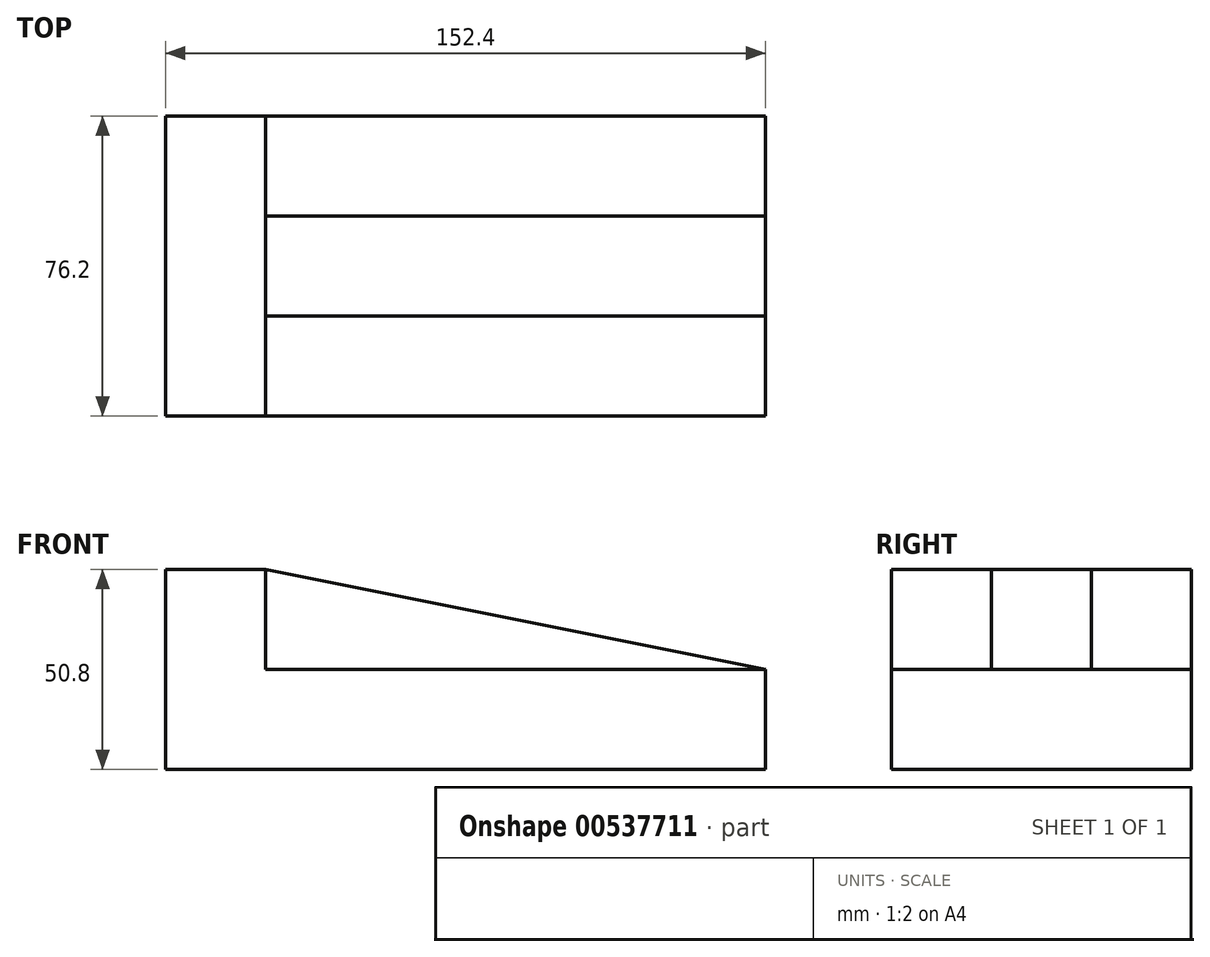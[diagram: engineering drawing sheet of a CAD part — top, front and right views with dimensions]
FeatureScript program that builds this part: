
annotation { "Feature Type Name" : "Feature", "Feature Type Description" : "" }
export const myFeature = defineFeature(function(context is Context, id is Id, definition is map)
    precondition{}
    {
        {
            var Q0;
            Q0=qCreatedBy(makeId("Front.planeOp"),FACE);
            var sketch = newSketch(context, id + "F0", { "sketchPlane" : qUnion([Q0])});
            skLineSegment(sketch, "E0.bottom", {"start": v(-87.33, 25.9) * mm, "end": v(-61.93, 25.9) * mm});
            skLineSegment(sketch, "E0.top", {"start": v(-87.33, -24.9) * mm, "end": v(65.07, -24.9) * mm});
            skLineSegment(sketch, "E0.left", {"start": v(-87.33, 25.9) * mm, "end": v(-87.33, -24.9) * mm});
            skLineSegment(sketch, "E0.right", {"start": v(65.07, 0.5) * mm, "end": v(65.07, -24.9) * mm});
            skLineSegment(sketch, "E1", {"start": v(65.07, -24.9) * mm, "end": v(-61.93, -24.9) * mm});
            skLineSegment(sketch, "E2", {"start": v(-61.93, 0.5) * mm, "end": v(-61.93, 25.9) * mm});
            skLineSegment(sketch, "E3", {"start": v(-87.33, -24.9) * mm, "end": v(-87.33, 0.5) * mm});
            skLineSegment(sketch, "E4", {"start": v(-61.93, 0.5) * mm, "end": v(65.07, 0.5) * mm});
            skLineSegment(sketch, "E5", {"start": v(-61.93, 25.9) * mm, "end": v(65.07, 0.5) * mm});
            skSolve(sketch);
        }
        {
            var Q0;
            Q0=makeQuery(id+"F0.imprint","IMPRINT",FACE,{"disambiguationData":[TD([[makeQuery(id+"F0.imprint","IMPRINT",EDGE,{"derivedFrom":sQuery(id+"F0.wireOp",EDGE,"E0.bottom")}),-1.0]])]});
            extrude(context, id + "F1", {"entities" : qUnion([Q0]), "oppositeDirection" : true, "depth" : 50.8 * mm, "offsetDistance" : 25.4 * mm});
        }
        {
            var Q0;
            Q0=makeQuery(id+"F0.imprint","IMPRINT",FACE,{"disambiguationData":[TD([[makeQuery(id+"F0.imprint","IMPRINT",EDGE,{"derivedFrom":sQuery(id+"F0.wireOp",EDGE,"E0.bottom")}),-1.0]])]});
            extrude(context, id + "F2", {"entities" : qUnion([Q0]), "operationType" : NewBodyOperationType.ADD, "depth" : 25.4 * mm, "offsetDistance" : 25.4 * mm});
        }
        {
            var Q0;
            Q0=makeQuery(id+"F0.imprint","IMPRINT",FACE,{"disambiguationData":[TD([[makeQuery(id+"F0.imprint","IMPRINT",EDGE,{"derivedFrom":sQuery(id+"F0.wireOp",EDGE,"E2")}),-1.0]])]});
            extrude(context, id + "F3", {"entities" : qUnion([Q0]), "operationType" : NewBodyOperationType.ADD, "oppositeDirection" : true, "depth" : 25.4 * mm, "offsetDistance" : 25.4 * mm});
        }
    });
